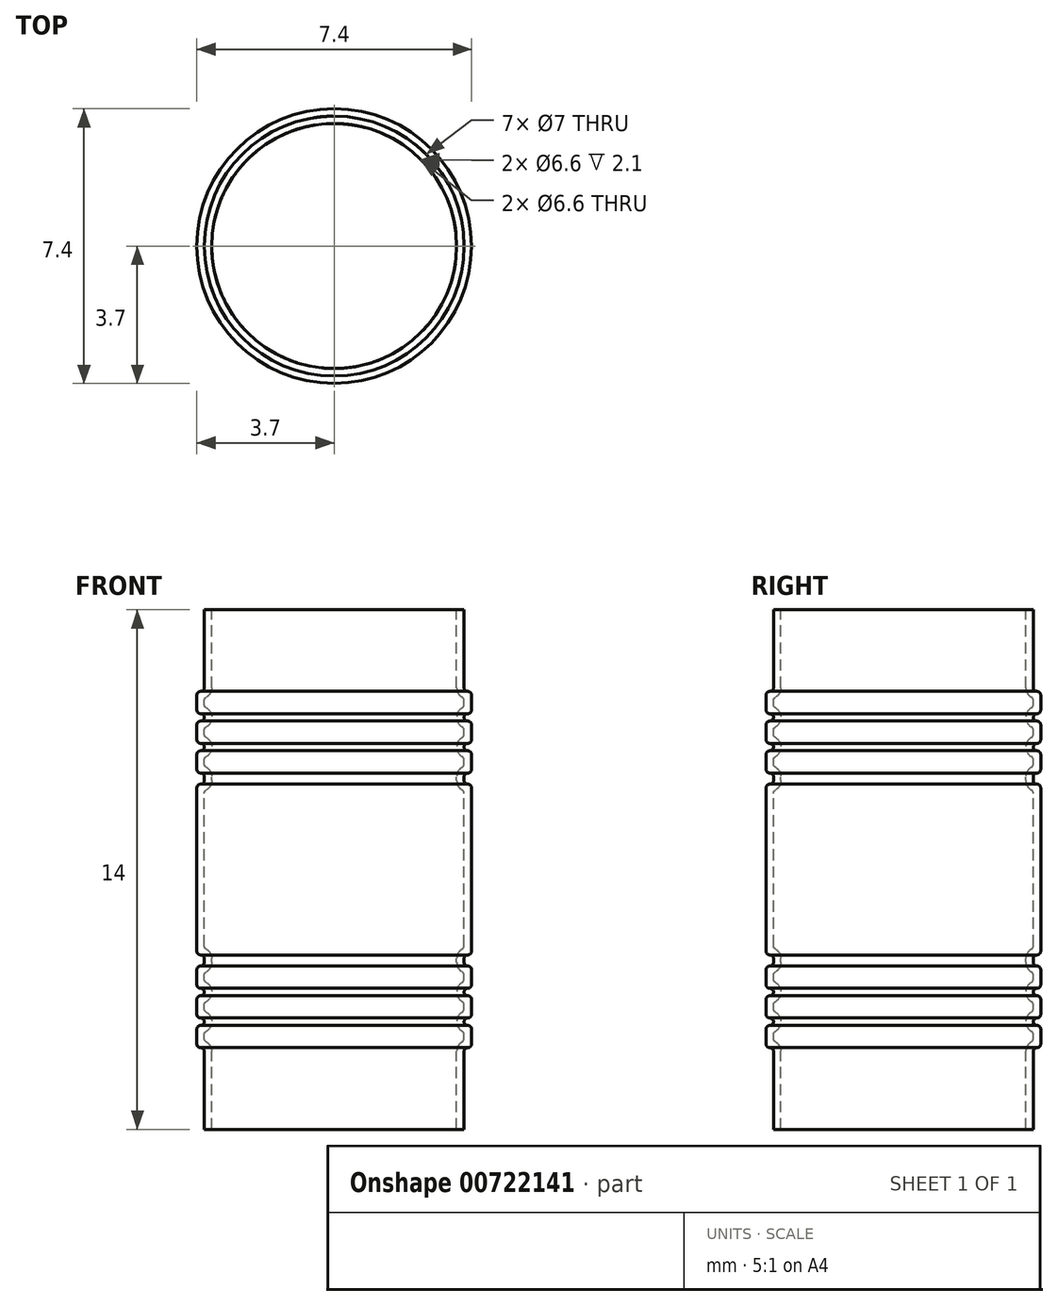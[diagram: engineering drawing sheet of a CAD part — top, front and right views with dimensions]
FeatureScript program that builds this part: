
annotation { "Feature Type Name" : "Feature", "Feature Type Description" : "" }
export const myFeature = defineFeature(function(context is Context, id is Id, definition is map)
    precondition{}
    {
        {
            var Q0;
            Q0=qCreatedBy(makeId("Front.planeOp"),FACE);
            var sketch = newSketch(context, id + "F0", { "sketchPlane" : qUnion([Q0])});
            skLineSegment(sketch, "E0", {"start": v(0, 60) * mm, "end": v(0, -60) * mm});
            skLineSegment(sketch, "E1", {"start": v(-70, 0) * mm, "end": v(70, 0) * mm});
            skLineSegment(sketch, "E2", {"start": v(-3.7, 4.8) * mm, "end": v(-3.7, 9.2) * mm});
            skLineSegment(sketch, "E3", {"start": v(-3.5, 14) * mm, "end": v(-3.3, 14) * mm});
            skLineSegment(sketch, "E4", {"start": v(-3.5, 0) * mm, "end": v(-3.3, 0) * mm});
            skLineSegment(sketch, "E5", {"start": v(-3.5, 12) * mm, "end": v(-3.5, 11.9) * mm});
            skLineSegment(sketch, "E6", {"start": v(-3.7, 11.7) * mm, "end": v(-3.7, 11.3) * mm});
            skLineSegment(sketch, "E7", {"start": v(-3.7, 10.9) * mm, "end": v(-3.7, 10.5) * mm});
            skLineSegment(sketch, "E8", {"start": v(-3.5, 9.5) * mm, "end": v(-3.5, 9.4) * mm});
            skLineSegment(sketch, "E9", {"start": v(-3.7, 10.1) * mm, "end": v(-3.7, 9.7) * mm});
            skArc(sketch, "E10", {"start": v(-3.6, 11.8) * mm, "mid": v(-3.53, 11.83) * mm, "end": v(-3.5, 11.9) * mm});
            skArc(sketch, "E11", {"start": v(-3.6, 11.8) * mm, "mid": v(-3.67, 11.77) * mm, "end": v(-3.7, 11.7) * mm});
            skArc(sketch, "E12", {"start": v(-3.7, 11.3) * mm, "mid": v(-3.67, 11.23) * mm, "end": v(-3.6, 11.2) * mm});
            skArc(sketch, "E13", {"start": v(-3.5, 11.1) * mm, "mid": v(-3.53, 11.17) * mm, "end": v(-3.6, 11.2) * mm});
            skArc(sketch, "E14", {"start": v(-3.6, 11) * mm, "mid": v(-3.53, 11.03) * mm, "end": v(-3.5, 11.1) * mm});
            skArc(sketch, "E15", {"start": v(-3.6, 11) * mm, "mid": v(-3.67, 10.97) * mm, "end": v(-3.7, 10.9) * mm});
            skArc(sketch, "E16", {"start": v(-3.7, 10.5) * mm, "mid": v(-3.67, 10.43) * mm, "end": v(-3.6, 10.4) * mm});
            skArc(sketch, "E17", {"start": v(-3.5, 10.3) * mm, "mid": v(-3.53, 10.37) * mm, "end": v(-3.6, 10.4) * mm});
            skArc(sketch, "E18", {"start": v(-3.6, 10.2) * mm, "mid": v(-3.53, 10.23) * mm, "end": v(-3.5, 10.3) * mm});
            skArc(sketch, "E19", {"start": v(-3.6, 10.2) * mm, "mid": v(-3.67, 10.17) * mm, "end": v(-3.7, 10.1) * mm});
            skArc(sketch, "E20", {"start": v(-3.7, 9.7) * mm, "mid": v(-3.67, 9.63) * mm, "end": v(-3.6, 9.6) * mm});
            skArc(sketch, "E21", {"start": v(-3.5, 9.5) * mm, "mid": v(-3.53, 9.57) * mm, "end": v(-3.6, 9.6) * mm});
            skLineSegment(sketch, "E22", {"start": v(-3.5, 2) * mm, "end": v(-3.5, 2.1) * mm});
            skLineSegment(sketch, "E23", {"start": v(-3.7, 2.3) * mm, "end": v(-3.7, 2.7) * mm});
            skLineSegment(sketch, "E24", {"start": v(-3.7, 3.1) * mm, "end": v(-3.7, 3.5) * mm});
            skLineSegment(sketch, "E25", {"start": v(-3.5, 4.5) * mm, "end": v(-3.5, 4.6) * mm});
            skLineSegment(sketch, "E26", {"start": v(-3.7, 3.9) * mm, "end": v(-3.7, 4.3) * mm});
            skArc(sketch, "E27", {"start": v(-3.5, 2.1) * mm, "mid": v(-3.53, 2.17) * mm, "end": v(-3.6, 2.2) * mm});
            skArc(sketch, "E28", {"start": v(-3.7, 2.3) * mm, "mid": v(-3.67, 2.23) * mm, "end": v(-3.6, 2.2) * mm});
            skArc(sketch, "E29", {"start": v(-3.6, 2.8) * mm, "mid": v(-3.67, 2.77) * mm, "end": v(-3.7, 2.7) * mm});
            skArc(sketch, "E30", {"start": v(-3.6, 2.8) * mm, "mid": v(-3.53, 2.83) * mm, "end": v(-3.5, 2.9) * mm});
            skArc(sketch, "E31", {"start": v(-3.5, 2.9) * mm, "mid": v(-3.53, 2.97) * mm, "end": v(-3.6, 3) * mm});
            skArc(sketch, "E32", {"start": v(-3.7, 3.1) * mm, "mid": v(-3.67, 3.03) * mm, "end": v(-3.6, 3) * mm});
            skArc(sketch, "E33", {"start": v(-3.6, 3.6) * mm, "mid": v(-3.67, 3.57) * mm, "end": v(-3.7, 3.5) * mm});
            skArc(sketch, "E34", {"start": v(-3.6, 3.6) * mm, "mid": v(-3.53, 3.63) * mm, "end": v(-3.5, 3.7) * mm});
            skArc(sketch, "E35", {"start": v(-3.5, 3.7) * mm, "mid": v(-3.53, 3.77) * mm, "end": v(-3.6, 3.8) * mm});
            skArc(sketch, "E36", {"start": v(-3.7, 3.9) * mm, "mid": v(-3.67, 3.83) * mm, "end": v(-3.6, 3.8) * mm});
            skArc(sketch, "E37", {"start": v(-3.6, 4.4) * mm, "mid": v(-3.67, 4.37) * mm, "end": v(-3.7, 4.3) * mm});
            skArc(sketch, "E38", {"start": v(-3.6, 4.4) * mm, "mid": v(-3.53, 4.43) * mm, "end": v(-3.5, 4.5) * mm});
            skLineSegment(sketch, "E39", {"start": v(-3.5, 14) * mm, "end": v(-3.5, 12) * mm});
            skLineSegment(sketch, "E40", {"start": v(-3.5, 2) * mm, "end": v(-3.5, 0) * mm});
            skArc(sketch, "E41", {"start": v(-3.5, 4.6) * mm, "mid": v(-3.53, 4.67) * mm, "end": v(-3.6, 4.7) * mm});
            skArc(sketch, "E42", {"start": v(-3.7, 4.8) * mm, "mid": v(-3.67, 4.73) * mm, "end": v(-3.6, 4.7) * mm});
            skArc(sketch, "E43", {"start": v(-3.6, 9.3) * mm, "mid": v(-3.67, 9.27) * mm, "end": v(-3.7, 9.2) * mm});
            skArc(sketch, "E44", {"start": v(-3.6, 9.3) * mm, "mid": v(-3.53, 9.33) * mm, "end": v(-3.5, 9.4) * mm});
            skLineSegment(sketch, "E45", {"start": v(-3.3, 14) * mm, "end": v(-3.3, 11.9) * mm});
            skArc(sketch, "E46", {"start": v(-3.45, 11.64) * mm, "mid": v(-3.34, 11.75) * mm, "end": v(-3.3, 11.9) * mm});
            skArc(sketch, "E47", {"start": v(-3.3, 11.1) * mm, "mid": v(-3.34, 11.25) * mm, "end": v(-3.45, 11.36) * mm});
            skLineSegment(sketch, "E48", {"start": v(-3.5, 11.55) * mm, "end": v(-3.5, 11.45) * mm});
            skArc(sketch, "E49", {"start": v(-3.45, 11.64) * mm, "mid": v(-3.49, 11.6) * mm, "end": v(-3.5, 11.55) * mm});
            skArc(sketch, "E50", {"start": v(-3.5, 11.45) * mm, "mid": v(-3.49, 11.4) * mm, "end": v(-3.45, 11.36) * mm});
            skArc(sketch, "E51", {"start": v(-3.45, 10.84) * mm, "mid": v(-3.34, 10.95) * mm, "end": v(-3.3, 11.1) * mm});
            skArc(sketch, "E52", {"start": v(-3.3, 10.3) * mm, "mid": v(-3.34, 10.45) * mm, "end": v(-3.45, 10.56) * mm});
            skArc(sketch, "E53", {"start": v(-3.45, 10.04) * mm, "mid": v(-3.34, 10.15) * mm, "end": v(-3.3, 10.3) * mm});
            skLineSegment(sketch, "E54", {"start": v(-3.5, 9.95) * mm, "end": v(-3.5, 9.85) * mm});
            skArc(sketch, "E55", {"start": v(-3.3, 9.5) * mm, "mid": v(-3.34, 9.65) * mm, "end": v(-3.45, 9.76) * mm});
            skArc(sketch, "E56", {"start": v(-3.45, 9.14) * mm, "mid": v(-3.34, 9.25) * mm, "end": v(-3.3, 9.4) * mm});
            skLineSegment(sketch, "E57", {"start": v(-3.3, 9.5) * mm, "end": v(-3.3, 9.4) * mm});
            skLineSegment(sketch, "E58", {"start": v(-3.5, 10.75) * mm, "end": v(-3.5, 10.65) * mm});
            skArc(sketch, "E59", {"start": v(-3.5, 10.65) * mm, "mid": v(-3.49, 10.6) * mm, "end": v(-3.45, 10.56) * mm});
            skArc(sketch, "E60", {"start": v(-3.45, 10.84) * mm, "mid": v(-3.49, 10.8) * mm, "end": v(-3.5, 10.75) * mm});
            skArc(sketch, "E61", {"start": v(-3.45, 10.04) * mm, "mid": v(-3.49, 10) * mm, "end": v(-3.5, 9.95) * mm});
            skArc(sketch, "E62", {"start": v(-3.5, 9.85) * mm, "mid": v(-3.49, 9.8) * mm, "end": v(-3.45, 9.76) * mm});
            skArc(sketch, "E63", {"start": v(-3.45, 9.14) * mm, "mid": v(-3.49, 9.1) * mm, "end": v(-3.5, 9.05) * mm});
            skLineSegment(sketch, "E64", {"start": v(-3.5, 0) * mm, "end": v(-3.5, 2) * mm});
            skLineSegment(sketch, "E65", {"start": v(-3.3, 0) * mm, "end": v(-3.3, 2.1) * mm});
            skArc(sketch, "E66", {"start": v(-3.3, 2.1) * mm, "mid": v(-3.34, 2.25) * mm, "end": v(-3.45, 2.36) * mm});
            skArc(sketch, "E67", {"start": v(-3.45, 2.64) * mm, "mid": v(-3.34, 2.75) * mm, "end": v(-3.3, 2.9) * mm});
            skLineSegment(sketch, "E68", {"start": v(-3.5, 2.45) * mm, "end": v(-3.5, 2.55) * mm});
            skArc(sketch, "E69", {"start": v(-3.5, 2.45) * mm, "mid": v(-3.49, 2.4) * mm, "end": v(-3.45, 2.36) * mm});
            skArc(sketch, "E70", {"start": v(-3.45, 2.64) * mm, "mid": v(-3.49, 2.6) * mm, "end": v(-3.5, 2.55) * mm});
            skArc(sketch, "E71", {"start": v(-3.3, 2.9) * mm, "mid": v(-3.34, 3.05) * mm, "end": v(-3.45, 3.16) * mm});
            skArc(sketch, "E72", {"start": v(-3.45, 3.44) * mm, "mid": v(-3.34, 3.55) * mm, "end": v(-3.3, 3.7) * mm});
            skArc(sketch, "E73", {"start": v(-3.3, 3.7) * mm, "mid": v(-3.34, 3.85) * mm, "end": v(-3.45, 3.96) * mm});
            skLineSegment(sketch, "E74", {"start": v(-3.5, 4.05) * mm, "end": v(-3.5, 4.15) * mm});
            skArc(sketch, "E75", {"start": v(-3.45, 4.24) * mm, "mid": v(-3.34, 4.35) * mm, "end": v(-3.3, 4.5) * mm});
            skArc(sketch, "E76", {"start": v(-3.3, 4.6) * mm, "mid": v(-3.34, 4.75) * mm, "end": v(-3.45, 4.86) * mm});
            skLineSegment(sketch, "E77", {"start": v(-3.3, 4.5) * mm, "end": v(-3.3, 4.6) * mm});
            skLineSegment(sketch, "E78", {"start": v(-3.5, 3.25) * mm, "end": v(-3.5, 3.35) * mm});
            skArc(sketch, "E79", {"start": v(-3.45, 3.44) * mm, "mid": v(-3.49, 3.4) * mm, "end": v(-3.5, 3.35) * mm});
            skArc(sketch, "E80", {"start": v(-3.5, 3.25) * mm, "mid": v(-3.49, 3.2) * mm, "end": v(-3.45, 3.16) * mm});
            skArc(sketch, "E81", {"start": v(-3.5, 4.05) * mm, "mid": v(-3.49, 4) * mm, "end": v(-3.45, 3.96) * mm});
            skArc(sketch, "E82", {"start": v(-3.45, 4.24) * mm, "mid": v(-3.49, 4.2) * mm, "end": v(-3.5, 4.15) * mm});
            skArc(sketch, "E83", {"start": v(-3.5, 4.95) * mm, "mid": v(-3.49, 4.9) * mm, "end": v(-3.45, 4.86) * mm});
            skLineSegment(sketch, "E84", {"start": v(-3.5, 9.05) * mm, "end": v(-3.5, 4.95) * mm});
            skSolve(sketch);
        }
        {
            var Q0;
            Q0=makeQuery(id+"F0.imprint","IMPRINT",FACE,{"disambiguationData":[TD([[makeQuery(id+"F0.imprint","IMPRINT",EDGE,{"derivedFrom":sQuery(id+"F0.wireOp",EDGE,"E2")}),-1.0]])]});
            var Q1;
            Q1=sQuery(id+"F0.wireOp",EDGE,"E0");
            revolve(context, id + "F1", {"surfaceOperationType" : NewSurfaceOperationType.NEW, "entities" : qUnion([Q0]), "axis" : qUnion([Q1]), "revolveType" : RevolveType.FULL});
        }
    });
